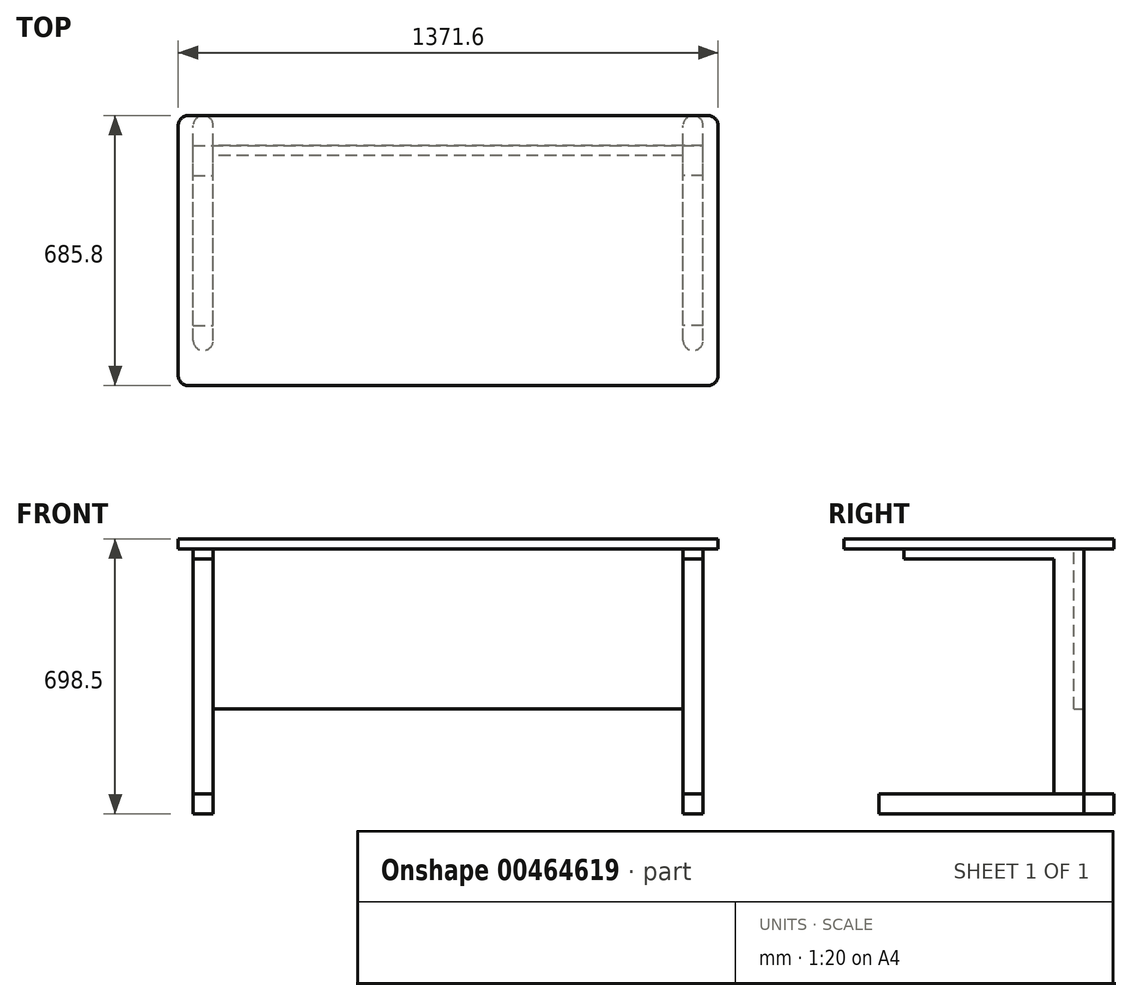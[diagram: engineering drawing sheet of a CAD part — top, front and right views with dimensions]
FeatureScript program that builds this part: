
annotation { "Feature Type Name" : "Feature", "Feature Type Description" : "" }
export const myFeature = defineFeature(function(context is Context, id is Id, definition is map)
    precondition{}
    {
        {
            var Q0;
            Q0=qCreatedBy(makeId("Top.planeOp"),FACE);
            var sketch = newSketch(context, id + "F0", { "sketchPlane" : qUnion([Q0])});
            skLineSegment(sketch, "E0.bottom", {"start": v(-680.27, -274.95) * mm, "end": v(640.53, -274.95) * mm});
            skLineSegment(sketch, "E0.top", {"start": v(-680.27, 410.85) * mm, "end": v(640.53, 410.85) * mm});
            skLineSegment(sketch, "E0.left", {"start": v(-705.67, -249.55) * mm, "end": v(-705.67, 385.45) * mm});
            skLineSegment(sketch, "E0.right", {"start": v(665.93, -249.55) * mm, "end": v(665.93, 385.45) * mm});
            skPoint(sketch, "E1.visualSharp", {"position": v(-705.67, 410.85) * mm});
            skArc(sketch, "E1.filletArc", {"start": v(-680.27, 410.85) * mm, "mid": v(-698.23, 403.42) * mm, "end": v(-705.67, 385.45) * mm});
            skPoint(sketch, "E2.visualSharp", {"position": v(665.93, 410.85) * mm});
            skArc(sketch, "E2.filletArc", {"start": v(665.93, 385.45) * mm, "mid": v(658.49, 403.42) * mm, "end": v(640.53, 410.85) * mm});
            skPoint(sketch, "E3.visualSharp", {"position": v(665.93, -274.95) * mm});
            skArc(sketch, "E3.filletArc", {"start": v(640.53, -274.95) * mm, "mid": v(658.49, -267.5) * mm, "end": v(665.93, -249.55) * mm});
            skPoint(sketch, "E4.visualSharp", {"position": v(-705.67, -274.95) * mm});
            skArc(sketch, "E4.filletArc", {"start": v(-705.67, -249.55) * mm, "mid": v(-698.23, -267.5) * mm, "end": v(-680.27, -274.95) * mm});
            skSolve(sketch);
        }
        {
            var Q0;
            Q0=makeQuery(id+"F0.imprint","IMPRINT",FACE,{"disambiguationData":[TD([[makeQuery(id+"F0.imprint","IMPRINT",EDGE,{"derivedFrom":sQuery(id+"F0.wireOp",EDGE,"E0.bottom")}),1.0]])]});
            extrude(context, id + "F1", {"entities" : qUnion([Q0]), "oppositeDirection" : true, "depth" : 25.4 * mm});
        }
        {
            var Q0;
            Q0=makeQuery(id+"F1.opExtrude","CAP_FACE",FACE,{"disambiguationData":[OSD([sQuery(id+"F0.wireOp",EDGE,"E0.bottom"),sQuery(id+"F0.wireOp",EDGE,"E0.top"),sQuery(id+"F0.wireOp",EDGE,"E0.left"),sQuery(id+"F0.wireOp",EDGE,"E0.right"),sQuery(id+"F0.wireOp",EDGE,"E1.filletArc"),sQuery(id+"F0.wireOp",EDGE,"E2.filletArc"),sQuery(id+"F0.wireOp",EDGE,"E3.filletArc"),sQuery(id+"F0.wireOp",EDGE,"E4.filletArc")])],"isStart":false});
            var sketch = newSketch(context, id + "F2", { "sketchPlane" : qUnion([Q0])});
            skLineSegment(sketch, "E5.bottom", {"start": v(-667.57, 122.55) * mm, "end": v(-616.77, 122.55) * mm});
            skLineSegment(sketch, "E5.top", {"start": v(-667.57, -258.45) * mm, "end": v(-616.77, -258.45) * mm});
            skLineSegment(sketch, "E5.left", {"start": v(-667.57, 122.55) * mm, "end": v(-667.57, -258.45) * mm});
            skLineSegment(sketch, "E5.right", {"start": v(-616.77, 122.55) * mm, "end": v(-616.77, -258.45) * mm});
            skLineSegment(sketch, "E6", {"start": v(-19.87, 274.95) * mm, "end": v(-19.87, -410.85) * mm});
            skLineSegment(sketch, "E7.MirrorCS", {"start": v(577.03, 122.55) * mm, "end": v(577.03, -258.45) * mm});
            skLineSegment(sketch, "E8.MirrorCS", {"start": v(627.83, 122.55) * mm, "end": v(627.83, -258.45) * mm});
            skLineSegment(sketch, "E9.MirrorCS", {"start": v(627.83, 122.55) * mm, "end": v(577.03, 122.55) * mm});
            skLineSegment(sketch, "E10.MirrorCS", {"start": v(627.83, -258.45) * mm, "end": v(577.03, -258.45) * mm});
            skSolve(sketch);
        }
        {
            var Q0;
            Q0 = qSketchRegion(id + "F2", true);
            extrude(context, id + "F3", {"entities" : qUnion([Q0]), "operationType" : NewBodyOperationType.ADD, "depth" : 25.4 * mm});
        }
        {
            var Q0;
            Q0 = qSketchRegion(id + "F2", true);
            extrude(context, id + "F4", {"entities" : qUnion([Q0]), "operationType" : NewBodyOperationType.ADD, "depth" : 25.4 * mm});
        }
        {
            var Q0;
            Q0=makeQuery(id+"F1.opExtrude","CAP_FACE",FACE,{"disambiguationData":[OSD([sQuery(id+"F0.wireOp",EDGE,"E0.bottom"),sQuery(id+"F0.wireOp",EDGE,"E0.top"),sQuery(id+"F0.wireOp",EDGE,"E0.left"),sQuery(id+"F0.wireOp",EDGE,"E0.right"),sQuery(id+"F0.wireOp",EDGE,"E1.filletArc"),sQuery(id+"F0.wireOp",EDGE,"E2.filletArc"),sQuery(id+"F0.wireOp",EDGE,"E3.filletArc"),sQuery(id+"F0.wireOp",EDGE,"E4.filletArc")])],"isStart":false});
            var sketch = newSketch(context, id + "F5", { "sketchPlane" : qUnion([Q0])});
            skLineSegment(sketch, "E11.bottom", {"start": v(-667.57, -258.45) * mm, "end": v(-616.77, -258.45) * mm});
            skLineSegment(sketch, "E11.top", {"start": v(-667.57, -309.25) * mm, "end": v(-616.77, -309.25) * mm});
            skLineSegment(sketch, "E11.left", {"start": v(-667.57, -258.45) * mm, "end": v(-667.57, -309.25) * mm});
            skLineSegment(sketch, "E11.right", {"start": v(-616.77, -258.45) * mm, "end": v(-616.77, -309.25) * mm});
            skLineSegment(sketch, "E12", {"start": v(-19.87, 274.95) * mm, "end": v(-19.87, -410.85) * mm});
            skLineSegment(sketch, "E13.MirrorCS", {"start": v(627.83, -258.45) * mm, "end": v(577.03, -258.45) * mm});
            skLineSegment(sketch, "E14.MirrorCS", {"start": v(627.83, -309.25) * mm, "end": v(577.03, -309.25) * mm});
            skLineSegment(sketch, "E15.MirrorCS", {"start": v(577.03, -258.45) * mm, "end": v(577.03, -309.25) * mm});
            skLineSegment(sketch, "E16.MirrorCS", {"start": v(627.83, -258.45) * mm, "end": v(627.83, -309.25) * mm});
            skSolve(sketch);
        }
        {
            var Q0;
            Q0=makeQuery(id+"F5.imprint","IMPRINT",FACE,{"disambiguationData":[TD([[makeQuery(id+"F5.imprint","IMPRINT",EDGE,{"derivedFrom":sQuery(id+"F5.wireOp",EDGE,"E11.bottom")}),-1.0]])]});
            var Q1;
            Q1=makeQuery(id+"F5.imprint","IMPRINT",FACE,{"disambiguationData":[TD([[makeQuery(id+"F5.imprint","IMPRINT",EDGE,{"derivedFrom":sQuery(id+"F5.wireOp",EDGE,"E13.MirrorCS")}),1.0]])]});
            extrude(context, id + "F6", {"entities" : qUnion([Q0, Q1]), "operationType" : NewBodyOperationType.ADD, "depth" : 622.3 * mm});
        }
        {
            var Q0;
            Q0=makeQuery(id+"F1.opExtrude","CAP_FACE",FACE,{"disambiguationData":[OSD([sQuery(id+"F0.wireOp",EDGE,"E0.bottom"),sQuery(id+"F0.wireOp",EDGE,"E0.top"),sQuery(id+"F0.wireOp",EDGE,"E0.left"),sQuery(id+"F0.wireOp",EDGE,"E0.right"),sQuery(id+"F0.wireOp",EDGE,"E1.filletArc"),sQuery(id+"F0.wireOp",EDGE,"E2.filletArc"),sQuery(id+"F0.wireOp",EDGE,"E3.filletArc"),sQuery(id+"F0.wireOp",EDGE,"E4.filletArc")])],"isStart":false});
            var sketch = newSketch(context, id + "F7", { "sketchPlane" : qUnion([Q0])});
            skLineSegment(sketch, "E17.bottom", {"start": v(-667.57, -309.25) * mm, "end": v(-616.77, -309.25) * mm});
            skLineSegment(sketch, "E17.top", {"start": v(-667.57, -334.65) * mm, "end": v(-616.77, -334.65) * mm});
            skLineSegment(sketch, "E17.left", {"start": v(-667.57, -309.25) * mm, "end": v(-667.57, -334.65) * mm});
            skLineSegment(sketch, "E17.right", {"start": v(-616.77, -309.25) * mm, "end": v(-616.77, -334.65) * mm});
            skLineSegment(sketch, "E18", {"start": v(-19.87, 274.95) * mm, "end": v(-19.87, -410.85) * mm});
            skLineSegment(sketch, "E19.MirrorCS", {"start": v(627.83, -309.25) * mm, "end": v(577.03, -309.25) * mm});
            skLineSegment(sketch, "E20.MirrorCS", {"start": v(577.03, -309.25) * mm, "end": v(577.03, -334.65) * mm});
            skLineSegment(sketch, "E21.MirrorCS", {"start": v(627.83, -334.65) * mm, "end": v(577.03, -334.65) * mm});
            skLineSegment(sketch, "E22.MirrorCS", {"start": v(627.83, -309.25) * mm, "end": v(627.83, -334.65) * mm});
            skSolve(sketch);
        }
        {
            var Q0;
            Q0 = qSketchRegion(id + "F7", true);
            extrude(context, id + "F8", {"entities" : qUnion([Q0]), "operationType" : NewBodyOperationType.ADD, "depth" : 622.3 * mm});
        }
        {
            var Q0;
            Q0=makeQuery(id+"F8.boolean.opBoolean","MERGE",FACE,{"derivedFrom":[makeQuery(id+"F6.opExtrude","CAP_FACE",FACE,{"disambiguationData":[OSD([sQuery(id+"F5.wireOp",EDGE,"E11.bottom"),sQuery(id+"F5.wireOp",EDGE,"E11.top"),sQuery(id+"F5.wireOp",EDGE,"E11.left"),sQuery(id+"F5.wireOp",EDGE,"E11.right")])],"isStart":false}),makeQuery(id+"F8.opExtrude","CAP_FACE",FACE,{"disambiguationData":[OSD([sQuery(id+"F7.wireOp",EDGE,"E17.bottom"),sQuery(id+"F7.wireOp",EDGE,"E17.top"),sQuery(id+"F7.wireOp",EDGE,"E17.left"),sQuery(id+"F7.wireOp",EDGE,"E17.right")])],"isStart":false})]});
            var sketch = newSketch(context, id + "F9", { "sketchPlane" : qUnion([Q0])});
            skLineSegment(sketch, "E23.bottom", {"start": v(-667.57, -334.65) * mm, "end": v(-616.77, -334.65) * mm});
            skLineSegment(sketch, "E23.top", {"start": v(-642.17, -410.85) * mm, "end": v(-642.17, -410.85) * mm});
            skLineSegment(sketch, "E23.left", {"start": v(-667.57, -334.65) * mm, "end": v(-667.57, -385.45) * mm});
            skLineSegment(sketch, "E23.right", {"start": v(-616.77, -334.65) * mm, "end": v(-616.77, -385.45) * mm});
            skPoint(sketch, "E24.visualSharp", {"position": v(-667.57, -410.85) * mm});
            skArc(sketch, "E24.filletArc", {"start": v(-667.57, -385.45) * mm, "mid": v(-660.13, -403.42) * mm, "end": v(-642.17, -410.85) * mm});
            skPoint(sketch, "E25.visualSharp", {"position": v(-616.77, -410.85) * mm});
            skArc(sketch, "E25.filletArc", {"start": v(-642.17, -410.85) * mm, "mid": v(-624.21, -403.42) * mm, "end": v(-616.77, -385.45) * mm});
            skSolve(sketch);
        }
        {
            var Q0;
            Q0 = qSketchRegion(id + "F9", true);
            extrude(context, id + "F10", {"entities" : qUnion([Q0]), "depth" : 50.8 * mm});
        }
        {
            var Q0;
            Q0=makeQuery(id+"F8.boolean.opBoolean","MERGE",FACE,{"derivedFrom":[makeQuery(id+"F6.opExtrude","CAP_FACE",FACE,{"disambiguationData":[OSD([sQuery(id+"F5.wireOp",EDGE,"E11.bottom"),sQuery(id+"F5.wireOp",EDGE,"E11.top"),sQuery(id+"F5.wireOp",EDGE,"E11.left"),sQuery(id+"F5.wireOp",EDGE,"E11.right")])],"isStart":false}),makeQuery(id+"F8.opExtrude","CAP_FACE",FACE,{"disambiguationData":[OSD([sQuery(id+"F7.wireOp",EDGE,"E17.bottom"),sQuery(id+"F7.wireOp",EDGE,"E17.top"),sQuery(id+"F7.wireOp",EDGE,"E17.left"),sQuery(id+"F7.wireOp",EDGE,"E17.right")])],"isStart":false})]});
            var sketch = newSketch(context, id + "F11", { "sketchPlane" : qUnion([Q0])});
            skPoint(sketch, "E26.oppositeSnap0", {"position": v(-616.77, -296.55) * mm});
            skLineSegment(sketch, "E26.bottom", {"start": v(-667.57, -334.65) * mm, "end": v(-616.77, -334.65) * mm});
            skLineSegment(sketch, "E26.top", {"start": v(-642.17, 186.05) * mm, "end": v(-642.17, 186.05) * mm});
            skLineSegment(sketch, "E26.left", {"start": v(-667.57, -334.65) * mm, "end": v(-667.57, 160.65) * mm});
            skLineSegment(sketch, "E26.right", {"start": v(-616.77, -334.65) * mm, "end": v(-616.77, 160.65) * mm});
            skPoint(sketch, "E27.visualSharp", {"position": v(-667.57, 186.05) * mm});
            skArc(sketch, "E27.filletArc", {"start": v(-642.17, 186.05) * mm, "mid": v(-660.13, 178.6) * mm, "end": v(-667.57, 160.65) * mm});
            skPoint(sketch, "E28.visualSharp", {"position": v(-616.77, 186.05) * mm});
            skArc(sketch, "E28.filletArc", {"start": v(-616.77, 160.65) * mm, "mid": v(-624.21, 178.6) * mm, "end": v(-642.17, 186.05) * mm});
            skSolve(sketch);
        }
        {
            var Q0;
            Q0 = qSketchRegion(id + "F11", true);
            extrude(context, id + "F12", {"entities" : qUnion([Q0]), "depth" : 50.8 * mm});
        }
        {
            var Q0;
            Q0=makeQuery(id+"F8.boolean.opBoolean","MERGE",FACE,{"derivedFrom":[makeQuery(id+"F6.opExtrude","CAP_FACE",FACE,{"disambiguationData":[OSD([sQuery(id+"F5.wireOp",EDGE,"E13.MirrorCS"),sQuery(id+"F5.wireOp",EDGE,"E14.MirrorCS"),sQuery(id+"F5.wireOp",EDGE,"E15.MirrorCS"),sQuery(id+"F5.wireOp",EDGE,"E16.MirrorCS")])],"isStart":false}),makeQuery(id+"F8.opExtrude","CAP_FACE",FACE,{"disambiguationData":[OSD([sQuery(id+"F7.wireOp",EDGE,"E19.MirrorCS"),sQuery(id+"F7.wireOp",EDGE,"E20.MirrorCS"),sQuery(id+"F7.wireOp",EDGE,"E21.MirrorCS"),sQuery(id+"F7.wireOp",EDGE,"E22.MirrorCS")])],"isStart":false})]});
            var sketch = newSketch(context, id + "F13", { "sketchPlane" : qUnion([Q0])});
            skLineSegment(sketch, "E29.bottom", {"start": v(577.03, -334.65) * mm, "end": v(627.83, -334.65) * mm});
            skLineSegment(sketch, "E29.top", {"start": v(602.43, -410.85) * mm, "end": v(602.43, -410.85) * mm});
            skLineSegment(sketch, "E29.left", {"start": v(577.03, -334.65) * mm, "end": v(577.03, -385.45) * mm});
            skLineSegment(sketch, "E29.right", {"start": v(627.83, -334.65) * mm, "end": v(627.83, -385.45) * mm});
            skPoint(sketch, "E30.visualSharp", {"position": v(577.03, -410.85) * mm});
            skArc(sketch, "E30.filletArc", {"start": v(577.03, -385.45) * mm, "mid": v(584.47, -403.42) * mm, "end": v(602.43, -410.85) * mm});
            skPoint(sketch, "E31.visualSharp", {"position": v(627.83, -410.85) * mm});
            skArc(sketch, "E31.filletArc", {"start": v(602.43, -410.85) * mm, "mid": v(620.39, -403.42) * mm, "end": v(627.83, -385.45) * mm});
            skSolve(sketch);
        }
        {
            var Q0;
            Q0 = qSketchRegion(id + "F13", true);
            extrude(context, id + "F14", {"entities" : qUnion([Q0]), "depth" : 50.8 * mm});
        }
        {
            var Q0;
            Q0=makeQuery(id+"F8.boolean.opBoolean","MERGE",FACE,{"derivedFrom":[makeQuery(id+"F6.opExtrude","CAP_FACE",FACE,{"disambiguationData":[OSD([sQuery(id+"F5.wireOp",EDGE,"E13.MirrorCS"),sQuery(id+"F5.wireOp",EDGE,"E14.MirrorCS"),sQuery(id+"F5.wireOp",EDGE,"E15.MirrorCS"),sQuery(id+"F5.wireOp",EDGE,"E16.MirrorCS")])],"isStart":false}),makeQuery(id+"F8.opExtrude","CAP_FACE",FACE,{"disambiguationData":[OSD([sQuery(id+"F7.wireOp",EDGE,"E19.MirrorCS"),sQuery(id+"F7.wireOp",EDGE,"E20.MirrorCS"),sQuery(id+"F7.wireOp",EDGE,"E21.MirrorCS"),sQuery(id+"F7.wireOp",EDGE,"E22.MirrorCS")])],"isStart":false})]});
            var sketch = newSketch(context, id + "F15", { "sketchPlane" : qUnion([Q0])});
            skLineSegment(sketch, "E32.bottom", {"start": v(577.03, -334.65) * mm, "end": v(627.83, -334.65) * mm});
            skLineSegment(sketch, "E32.top", {"start": v(602.43, 186.05) * mm, "end": v(602.43, 186.05) * mm});
            skLineSegment(sketch, "E32.left", {"start": v(577.03, -334.65) * mm, "end": v(577.03, 160.65) * mm});
            skLineSegment(sketch, "E32.right", {"start": v(627.83, -334.65) * mm, "end": v(627.83, 160.65) * mm});
            skPoint(sketch, "E33.visualSharp", {"position": v(577.03, 186.05) * mm});
            skArc(sketch, "E33.filletArc", {"start": v(602.43, 186.05) * mm, "mid": v(584.47, 178.6) * mm, "end": v(577.03, 160.65) * mm});
            skPoint(sketch, "E34.visualSharp", {"position": v(627.83, 186.05) * mm});
            skArc(sketch, "E34.filletArc", {"start": v(627.83, 160.65) * mm, "mid": v(620.39, 178.6) * mm, "end": v(602.43, 186.05) * mm});
            skSolve(sketch);
        }
        {
            var Q0;
            Q0 = qSketchRegion(id + "F15", true);
            extrude(context, id + "F16", {"entities" : qUnion([Q0]), "depth" : 50.8 * mm});
        }
        {
            var Q0;
            Q0=makeQuery(id+"F8.opExtrude","SWEPT_FACE",FACE,{"disambiguationData":[OSD([sQuery(id+"F7.wireOp",EDGE,"E21.MirrorCS")])]});
            var sketch = newSketch(context, id + "F17", { "sketchPlane" : qUnion([Q0])});
            skLineSegment(sketch, "E35.bottom", {"start": v(-577.03, -25.4) * mm, "end": v(616.77, -25.4) * mm});
            skLineSegment(sketch, "E35.top", {"start": v(-577.03, -431.8) * mm, "end": v(616.77, -431.8) * mm});
            skLineSegment(sketch, "E35.left", {"start": v(-577.03, -25.4) * mm, "end": v(-577.03, -431.8) * mm});
            skLineSegment(sketch, "E35.right", {"start": v(616.77, -25.4) * mm, "end": v(616.77, -431.8) * mm});
            skSolve(sketch);
        }
        {
            var Q0;
            Q0=makeQuery(id+"F17.imprint","IMPRINT",FACE,{"disambiguationData":[TD([[makeQuery(id+"F17.imprint","IMPRINT",EDGE,{"derivedFrom":sQuery(id+"F17.wireOp",EDGE,"E35.bottom")}),-1.0]])]});
            extrude(context, id + "F18", {"entities" : qUnion([Q0]), "operationType" : NewBodyOperationType.ADD, "oppositeDirection" : true, "depth" : 25.4 * mm});
        }
    });
